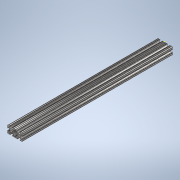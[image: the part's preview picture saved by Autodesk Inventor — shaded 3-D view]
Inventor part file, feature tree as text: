
AUTODESK INVENTOR PART (.ipt)
format: ipt  version: 2020 (Build 240168000, 168)  size: 350,208 bytes
history: native  units: in
note: dims shown in document units (in); Inventor stores cm internally (conversion verified against a paired STEP export)
features: sketch x2, extrude x1
ambient origin geometry x8: Origin, YZ Plane, XZ Plane, XY Plane, X Axis, Y Axis, Z Axis, Center Point
bodies: Solid1 (feature_tree)
feature tree (3):
  extrude  "Extrusion1"  [1 undecoded]
  sketch  "Sketch2"
  sketch  "Sketch1"  dims[d0=20.0in d1=0.0in]
note: 1 required parameter value undecoded (feature->parameter linkage not recoverable at this tier; creation-order binding heuristic only, values carry confidence <= 0.55)
